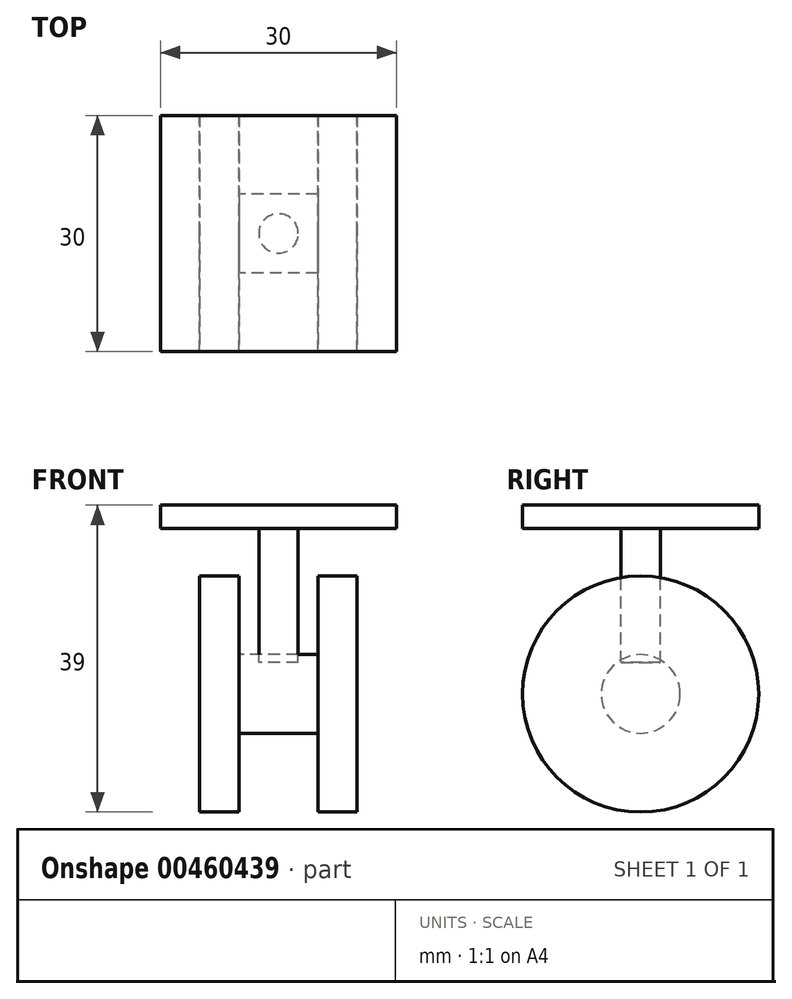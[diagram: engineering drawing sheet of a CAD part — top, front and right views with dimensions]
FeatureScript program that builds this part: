
annotation { "Feature Type Name" : "Feature", "Feature Type Description" : "" }
export const myFeature = defineFeature(function(context is Context, id is Id, definition is map)
    precondition{}
    {
        {
            var Q0;
            Q0=qCreatedBy(makeId("Top.planeOp"),FACE);
            var sketch = newSketch(context, id + "F0", { "sketchPlane" : qUnion([Q0])});
            skLineSegment(sketch, "E0.bottom", {"start": v(15, -15) * mm, "end": v(-15, -15) * mm});
            skLineSegment(sketch, "E0.top", {"start": v(15, 15) * mm, "end": v(-15, 15) * mm});
            skLineSegment(sketch, "E0.left", {"start": v(15, -15) * mm, "end": v(15, 15) * mm});
            skLineSegment(sketch, "E0.right", {"start": v(-15, -15) * mm, "end": v(-15, 15) * mm});
            skLineSegment(sketch, "E1", {"start": v(0, 15) * mm, "end": v(0, -15) * mm, "construction": true});
            skCircle(sketch, "E2", {"center": v(0, 0) * mm, "radius": 2.5 * mm});
            skSolve(sketch);
        }
        {
            var Q0;
            Q0=makeQuery(id+"F0.imprint","IMPRINT",FACE,{"disambiguationData":[TD([[makeQuery(id+"F0.imprint","IMPRINT",EDGE,{"derivedFrom":sQuery(id+"F0.wireOp",EDGE,"E0.bottom")}),-1.0]])]});
            var Q1;
            Q1=makeQuery(id+"F0.imprint","IMPRINT",FACE,{"disambiguationData":[TD([[makeQuery(id+"F0.imprint","IMPRINT",EDGE,{"derivedFrom":sQuery(id+"F0.wireOp",EDGE,"E2")}),1.0]])]});
            extrude(context, id + "F1", {"entities" : qUnion([Q0, Q1]), "oppositeDirection" : true, "depth" : 3 * mm});
        }
        {
            var Q0;
            Q0=makeQuery(id+"F0.imprint","IMPRINT",FACE,{"disambiguationData":[TD([[makeQuery(id+"F0.imprint","IMPRINT",EDGE,{"derivedFrom":sQuery(id+"F0.wireOp",EDGE,"E2")}),1.0]])]});
            extrude(context, id + "F2", {"entities" : qUnion([Q0]), "operationType" : NewBodyOperationType.ADD, "oppositeDirection" : true, "depth" : 20 * mm});
        }
        {
            var Q0;
            Q0=qCreatedBy(makeId("Front.planeOp"),FACE);
            var sketch = newSketch(context, id + "F3", { "sketchPlane" : qUnion([Q0])});
            skLineSegment(sketch, "E3", {"start": v(-10, -24) * mm, "end": v(10, -24) * mm});
            skLineSegment(sketch, "E4", {"start": v(10, -24) * mm, "end": v(10, -9) * mm});
            skLineSegment(sketch, "E5", {"start": v(10, -9) * mm, "end": v(5, -9) * mm});
            skLineSegment(sketch, "E6", {"start": v(5, -9) * mm, "end": v(5, -19) * mm});
            skLineSegment(sketch, "E7", {"start": v(5, -19) * mm, "end": v(-5, -19) * mm});
            skLineSegment(sketch, "E8", {"start": v(-5, -19) * mm, "end": v(-5, -9) * mm});
            skLineSegment(sketch, "E9", {"start": v(-5, -9) * mm, "end": v(-10, -9) * mm});
            skLineSegment(sketch, "E10", {"start": v(-10, -9) * mm, "end": v(-10, -24) * mm});
            skPoint(sketch, "E11", {"position": v(0, -19) * mm});
            skPoint(sketch, "E12", {"position": v(0, -24) * mm});
            skSolve(sketch);
        }
        {
            var Q0;
            Q0=makeQuery(id+"F3.imprint","IMPRINT",FACE,{"disambiguationData":[TD([[makeQuery(id+"F3.imprint","IMPRINT",EDGE,{"derivedFrom":sQuery(id+"F3.wireOp",EDGE,"E3")}),1.0]])]});
            var Q1;
            Q1=sQuery(id+"F3.wireOp",EDGE,"E3");
            revolve(context, id + "F4", {"entities" : qUnion([Q0]), "axis" : qUnion([Q1]), "revolveType" : RevolveType.FULL});
        }
    });
